# Revit family: Uno Suspended Lighting Fixture 1
name_source: partatom
category: Lighting Fixtures
revit_build: Autodesk Revit 2018 (Build: 20190510_1515(x64)
units: mm (PartAtom-declared; Revit-internal decimal feet)

## family parameters
Always vertical = Yes
Cut with Voids When Loaded = No
Host = Ceiling
Light Source = Yes
OmniClass Number = 23.80.70.11
OmniClass Title = Luminaries for Internal Lighting
Part Type = Normal
Room Calculation Point = No
Round Connector Dimension = Use Diameter
Shared = No

## types (36) — shared parameters
Aircraft Cable Suspension = Stainless Steel
Color Filter = 16777215
Dimming Lamp Color Temperature Shift = <None>
Emit from Line Length = 2' - 0"
Glass = Glass
Load = Other
Manufacturer = ARON
Poles = 1
Specification = http://www.aronlighting.com
Tilt Angle = 90.00°
URL = http://www.aronlighting.com

## per-type parameters (varying)
| type | 10FT | 12FT | 14FT | 16FT | 20FT A | 20FT B | 20FT C | 22FT A | 22FT B | 22FT C | 24 FT | 26FT | 28FT | 4FT TO 8FT | Apparent Load | Case | Length | Photometric Web File | Voltage |
| White 4FT | No | No | No | No | No | No | No | No | No | No | No | No | No | Yes | 0 VA | White | 4' - 0" | edge-suspended-b3.ies | 0 V |
| White 5FT | No | No | No | No | No | No | No | No | No | No | No | No | No | Yes | 0 VA | White | 5' - 0" | edge-suspended-b3.ies | 0 V |
| White 6FT | No | No | No | No | No | No | No | No | No | No | No | No | No | Yes | 0 VA | White | 6' - 0" | edge-suspended-b3.ies | 0 V |
| Black 7FT | No | No | No | No | No | No | No | No | No | No | No | No | No | Yes | 0 VA | Black | 7' - 0" | generic | 0 V |
| White 8FT | No | No | No | No | No | No | No | No | No | No | No | No | No | Yes | 0 VA | White | 8' - 0" | edge-suspended-b3.ies | 0 V |
| Black 10FT | Yes | No | No | No | No | No | No | No | No | No | No | No | No | No | 0 VA | Black | 4' - 0" | generic | 0 V |
| White 12FT | No | Yes | No | No | No | No | No | No | No | No | No | No | No | No | 0 VA | White | 4' - 0" | edge-suspended-b3.ies | 0 V |
| Black 14FT | No | No | Yes | No | No | No | No | No | No | No | No | No | No | No | 0 VA | Black | 4' - 0" | generic | 0 V |
| White 16FT | No | No | No | Yes | No | No | No | No | No | No | No | No | No | No | 0 VA | White | 4' - 0" | edge-suspended-b3.ies | 0 V |
| Black 20FT B | No | No | No | No | No | Yes | No | No | No | No | No | No | No | No | 0 VA | Black | 4' - 0" | edge-suspended-b3.ies | 0 V |
| Black 4FT | No | No | No | No | No | No | No | No | No | No | No | No | No | Yes | 120 VA | Black | 4' - 0" | edge-suspended-b3.ies | 120 V |
| Black 5FT | No | No | No | No | No | No | No | No | No | No | No | No | No | Yes | 0 VA | Black | 5' - 0" | generic | 0 V |
| Black 6FT | No | No | No | No | No | No | No | No | No | No | No | No | No | Yes | 0 VA | Black | 6' - 0" | generic | 0 V |
| White 7FT | No | No | No | No | No | No | No | No | No | No | No | No | No | Yes | 0 VA | White | 7' - 0" | edge-suspended-b3.ies | 0 V |
| Black 8FT | No | No | No | No | No | No | No | No | No | No | No | No | No | Yes | 0 VA | Black | 8' - 0" |  | 0 V |
| White 10FT | Yes | No | No | No | No | No | No | No | No | No | No | No | No | No | 0 VA | White | 4' - 0" | edge-suspended-b3.ies | 0 V |
| Black 12FT | No | Yes | No | No | No | No | No | No | No | No | No | No | No | No | 0 VA | Black | 4' - 0" | generic | 0 V |
| White 14FT | No | No | Yes | No | No | No | No | No | No | No | No | No | No | No | 0 VA | White | 4' - 0" | edge-suspended-b3.ies | 0 V |
| Black 16FT | No | No | No | Yes | No | No | No | No | No | No | No | No | No | No | 0 VA | Black | 4' - 0" | generic | 0 V |
| White 20FT B | No | No | No | No | No | Yes | No | No | No | No | No | No | No | No | 0 VA | White | 4' - 0" | edge-suspended-b3.ies | 0 V |
| White 20FT A | No | No | No | No | Yes | No | No | No | No | No | No | No | No | No | 0 VA | White | 4' - 0" | edge-suspended-b3.ies | 0 V |
| White 20FT C | No | No | No | No | No | No | Yes | No | No | No | No | No | No | No | 0 VA | White | 4' - 0" | edge-suspended-b3.ies | 0 V |
| Black 20FT A | No | No | No | No | Yes | No | No | No | No | No | No | No | No | No | 0 VA | Black | 4' - 0" | edge-suspended-b3.ies | 0 V |
| Black 20FT C | No | No | No | No | No | No | Yes | No | No | No | No | No | No | No | 0 VA | Black | 4' - 0" | edge-suspended-b3.ies | 0 V |
| Black 22FT A | No | No | No | No | No | No | No | Yes | No | No | No | No | No | No | 0 VA | Black | 4' - 0" |  | 0 V |
| Black 22FT B | No | No | No | No | No | No | No | No | Yes | No | No | No | No | No | 0 VA | Black | 4' - 0" |  | 0 V |
| Black 22FT C | No | No | No | No | No | No | No | No | No | Yes | No | No | No | No | 0 VA | Black | 4' - 0" |  | 0 V |
| Black 24FT | No | No | No | No | No | No | No | No | No | No | Yes | No | No | No | 0 VA | Black | 4' - 0" |  | 0 V |
| White 24FT | No | No | No | No | No | No | No | No | No | No | Yes | No | No | No | 0 VA | White | 4' - 0" | edge-suspended-b3.ies | 0 V |
| White 26FT | No | No | No | No | No | No | No | No | No | No | No | Yes | No | No | 0 VA | White | 4' - 0" | edge-suspended-b3.ies | 0 V |
| Black 26FT | No | No | No | No | No | No | No | No | No | No | No | Yes | No | No | 0 VA | Black | 4' - 0" |  | 0 V |
| Black 28FT | No | No | No | No | No | No | No | No | No | No | No | No | Yes | No | 0 VA | Black | 4' - 0" |  | 0 V |
| White 28FT | No | No | No | No | No | No | No | No | No | No | No | No | Yes | No | 0 VA | White | 4' - 0" | edge-suspended-b3.ies | 0 V |
| White 22FT C | No | No | No | No | No | No | No | No | No | Yes | No | No | No | No | 0 VA | White | 4' - 0" | edge-suspended-b3.ies | 0 V |
| White 22FT B | No | No | No | No | No | No | No | No | Yes | No | No | No | No | No | 0 VA | White | 4' - 0" | edge-suspended-b3.ies | 0 V |
| White 22FT A | No | No | No | No | No | No | No | Yes | No | No | No | No | No | No | 0 VA | White | 4' - 0" | edge-suspended-b3.ies | 0 V |

## geometry (parser evidence)
native form markers: Sweep x14
no freeform markers — native parametric forms only
